# Revit family: Building-IEC309Connections-GEWISS-44IB-INTERLOCKED-SOCKET-OUTLETS_IP44_WITH_BOTTOM_FUS
name_source: partatom
category: Apparecchi elettrici
revit_build: Autodesk Revit 2016 (Build: 20161004_0715(x64)
units: mm (PartAtom-declared; Revit-internal decimal feet)

## family parameters
Condiviso = No
Host = Muro
Mantenere orientamento annotazione = Sì
Numero OmniClass = 23.80.50.14
Punto di calcolo locali = No
Quota connettore circolare = Usa diametro
Sempre verticale = Sì
Taglio con vuoti quando caricato = No
Tipo di parte = Normale
Titolo OmniClass = Plug Connectors

## types (22) — shared parameters
Altezza da terra = 820 mm
Carico apparente = 0 VA
Catalogue = BUILDING
Catalogue Range = 44 IB
Classificazione carico = Altro
Electrocod = 2220
Frequency = 50/60 Hz
Fuse breacking capacity = > 50 kA
Glow Wire Test = 850 °C (active parts) - 650 °C (passive parts)
Glow wire test: = 850 °C (active parts) - 650 °C (passive parts)
IDF = 6ad67383-5a29-4481-a0b8-72c9e5411bd3
IDT = df42792c-0395-498e-ac0c-0b2d4cd197bd
IP degree = IP44
Immagine tipo = GW66032.jpg
Numero poli = 3
Operating temperature: = -25 +40 °C
Potenza = 500 V
Presa = GEWISS - NERO
Produttore = GEWISS S.p.A.
Protection = Fuse-holder base (CBF)
Rated frequency (Hz) = 50/60 Hz
SEO = Socket outlet
Shock resistance = IK08
Struttura = GEWISS - Grigio RAL - 7035
Technical sheet = https://www.gewiss.com
Thermo-pressure with ball = 125 °C (active parts) - 80 °C (passive parts)
Tipo Simbolo = PRESAINDPFUS : 3P
Typology = Horizontal
URL = https://www.gewiss.com
Version file RFA = 18.0
Vetro = GEWISS - vetro
With back-mounting box = Yes
Working temperature = -25 ÷ +40 °C

## per-type parameters (varying)
| type | Colour | Colour: | Descrizione | EAN code | Fuses holder | Modello | No. of poles | Number of poles | Rated current (A) | Rated current (In) | Rated voltage | Reference h |
| GW66044 - 32A 3P+N+E 500V H.INT.SOCK.O.W.B. 7H CBF | Black | Black | 32A 3P+N+E 500V H.INT.SOCK.O.W.B. 7H CBF | 8011564006225 | gG | GW66044 | 3P+N+E | 3P+N+E | 32 | 32 | 480-500V | 7 |
| GW66029 - 16A 2P+E 400V H.INT.SOCK.O.W.B. 9H CBF | Red | Red | 16A 2P+E 400V H.INT.SOCK.O.W.B. 9H CBF | 8011564005945 | E14 | GW66029 | 2P+E | 2P+E | 16 | 16 | 380-415V | 9 |
| GW66038 - 32A 3P+E 230V H.INT.SOCK.O.W.B. 9H CBF | Blue | Blue | 32A 3P+E 230V H.INT.SOCK.O.W.B. 9H CBF | 8011564006065 | E18 | GW66038 | 3P+E | 3P+E | 32 | 32 | 200-250V | 9 |
| GW66031 - 16A 3P+N+E 400V H.INT.SOCK.O.W.B. 6H CBF | Red | Red | 16A 3P+N+E 400V H.INT.SOCK.O.W.B. 6H CBF | 8011564005938 | E14 | GW66031 | 3P+N+E | 3P+N+E | 16 | 16 | 380-415V | 6 |
| GW66034 - 32A 2P+E 110V H.INT.SOCK.O.W.B. 4H CBF | Yellow | Yellow | 32A 2P+E 110V H.INT.SOCK.O.W.B. 4H CBF | 8011564006010 | E18 | GW66034 | 2P+E | 2P+E | 32 | 32 | 100-130V | 4 |
| GW66030 - 16A 3P+E 400V H.INT.SOCK.O.W.B. 6H CBF | Red | Red | 16A 3P+E 400V H.INT.SOCK.O.W.B. 6H CBF | 8011564005921 | E14 | GW66030 | 3P+E | 3P+E | 16 | 16 | 380-415V | 6 |
| GW66033 - 16A 3P+N+E 500V H.INT.SOCK.O.W.B. 7H CBF | Black | Black | 16A 3P+N+E 500V H.INT.SOCK.O.W.B. 7H CBF | 8011564005990 | gG | GW66033 | 3P+N+E | 3P+N+E | 16 | 16 | 480-500V | 7 |
| GW66042 - 32A 3P+N+E 400V H.INT.SOCK.O.W.B. 6H CBF | Red | Red | 32A 3P+N+E 400V H.INT.SOCK.O.W.B. 6H CBF | 8011564006034 | E18 | GW66042 | 3P+N+E | 3P+N+E | 32 | 32 | 380-415V | 6 |
| GW66036 - 32A 3P+N+E 110V H.INT.SOCK.O.W.B. 4H CBF | Yellow | Yellow | 32A 3P+N+E 110V H.INT.SOCK.O.W.B. 4H CBF | 8011564006089 | E18 | GW66036 | 3P+N+E | 3P+N+E | 32 | 32 | 100-130V | 4 |
| GW66024 - 16A 3P+E 110V H.INT.SOCK.O.W.B. 4H CBF | Yellow | Yellow | 16A 3P+E 110V H.INT.SOCK.O.W.B. 4H CBF | 8011564005952 | E14 | GW66024 | 3P+E | 3P+E | 16 | 16 | 100-130V | 4 |
| GW66039 - 32A 3P+N+E 230V H.INT.SOCK.O.W.B. 9H CBF | Blue | Blue | 32A 3P+N+E 230V H.INT.SOCK.O.W.B. 9H CBF | 8011564006119 | E18 | GW66039 | 3P+N+E | 3P+N+E | 32 | 32 | 200-250V | 9 |
| GW66025 - 16A 3P+N+E 110V H.INT.SOCK.O.W.B. 4H CBF | Yellow | Yellow | 16A 3P+N+E 110V H.INT.SOCK.O.W.B. 4H CBF | 8011564005976 | E14 | GW66025 | 3P+N+E | 3P+N+E | 16 | 16 | 100-130V | 4 |
| GW66043 - 32A 3P+E 500V H.INT.SOCK.O.W.B. 7H CBF | Black | Black | 32A 3P+E 500V H.INT.SOCK.O.W.B. 7H CBF | 8011564006072 | gG | GW66043 | 3P+E | 3P+E | 32 | 32 | 480-500V | 7 |
| GW66035 - 32A 3P+E 110V H.INT.SOCK.O.W.B. 4H CBF | Yellow | Yellow | 32A 3P+E 110V H.INT.SOCK.O.W.B. 4H CBF | 8011564006058 | E18 | GW66035 | 3P+E | 3P+E | 32 | 32 | 100-130V | 4 |
| GW66028 - 16A 3P+N+E 230V H.INT.SOCK.O.W.B. 9H CBF | Blue | Blue | 16A 3P+N+E 230V H.INT.SOCK.O.W.B. 9H CBF | 8011564005983 | E14 | GW66028 | 3P+N+E | 3P+N+E | 16 | 16 | 200-250V | 9 |
| GW66037 - 32A 2P+E 230V H.INT.SOCK.O.W.B. 6H CBF | Blue | Blue | 32A 2P+E 230V H.INT.SOCK.O.W.B. 6H CBF | 8011564006003 | E18 | GW66037 | 2P+E | 2P+E | 32 | 32 | 200-250V | 6 |
| GW66023 - 16A 2P+E 110V H.INT.SOCK.O.W.B. 4H CBF | Yellow | Yellow | 16A 2P+E 110V H.INT.SOCK.O.W.B. 4H CBF | 8011564005891 | E14 | GW66023 | 2P+E | 2P+E | 16 | 16 | 100-130V | 4 |
| GW66027 - 16A 3P+E 230V H.INT.SOCK.O.W.B. 9H CBF | Blue | Blue | 16A 3P+E 230V H.INT.SOCK.O.W.B. 9H CBF | 8011564005914 | E14 | GW66027 | 3P+E | 3P+E | 16 | 16 | 200-250V | 9 |
| GW66040 - 32A 2P+E 400V H.INT.SOCK.O.W.B. 9H CBF | Red | Red | 32A 2P+E 400V H.INT.SOCK.O.W.B. 9H CBF | 8011564006041 | E18 | GW66040 | 2P+E | 2P+E | 32 | 32 | 380-415V | 9 |
| GW66032 - 16A 3P+E 500V H.INT.SOCK.O.W.B. 7H CBF | Black | Black | 16A 3P+E 500V H.INT.SOCK.O.W.B. 7H CBF | 8011564005969 | gG | GW66032 | 3P+E | 3P+E | 16 | 16 | 480-500V | 7 |
| GW66041 - 32A 3P+E 400V H.INT.SOCK.O.W.B. 6H CBF | Red | Red | 32A 3P+E 400V H.INT.SOCK.O.W.B. 6H CBF | 8011564006027 | E18 | GW66041 | 3P+E | 3P+E | 32 | 32 | 380-415V | 6 |
| GW66026 - 16A 2P+E 230V H.INT.SOCK.O.W.B. 6H CBF | Blue | Blue | 16A 2P+E 230V H.INT.SOCK.O.W.B. 6H CBF | 8011564005907 | E14 | GW66026 | 2P+E | 2P+E | 16 | 16 | 200-250V | 6 |

## geometry (parser evidence)
native form markers: Blend x4, Sweep x2
no freeform markers — native parametric forms only
